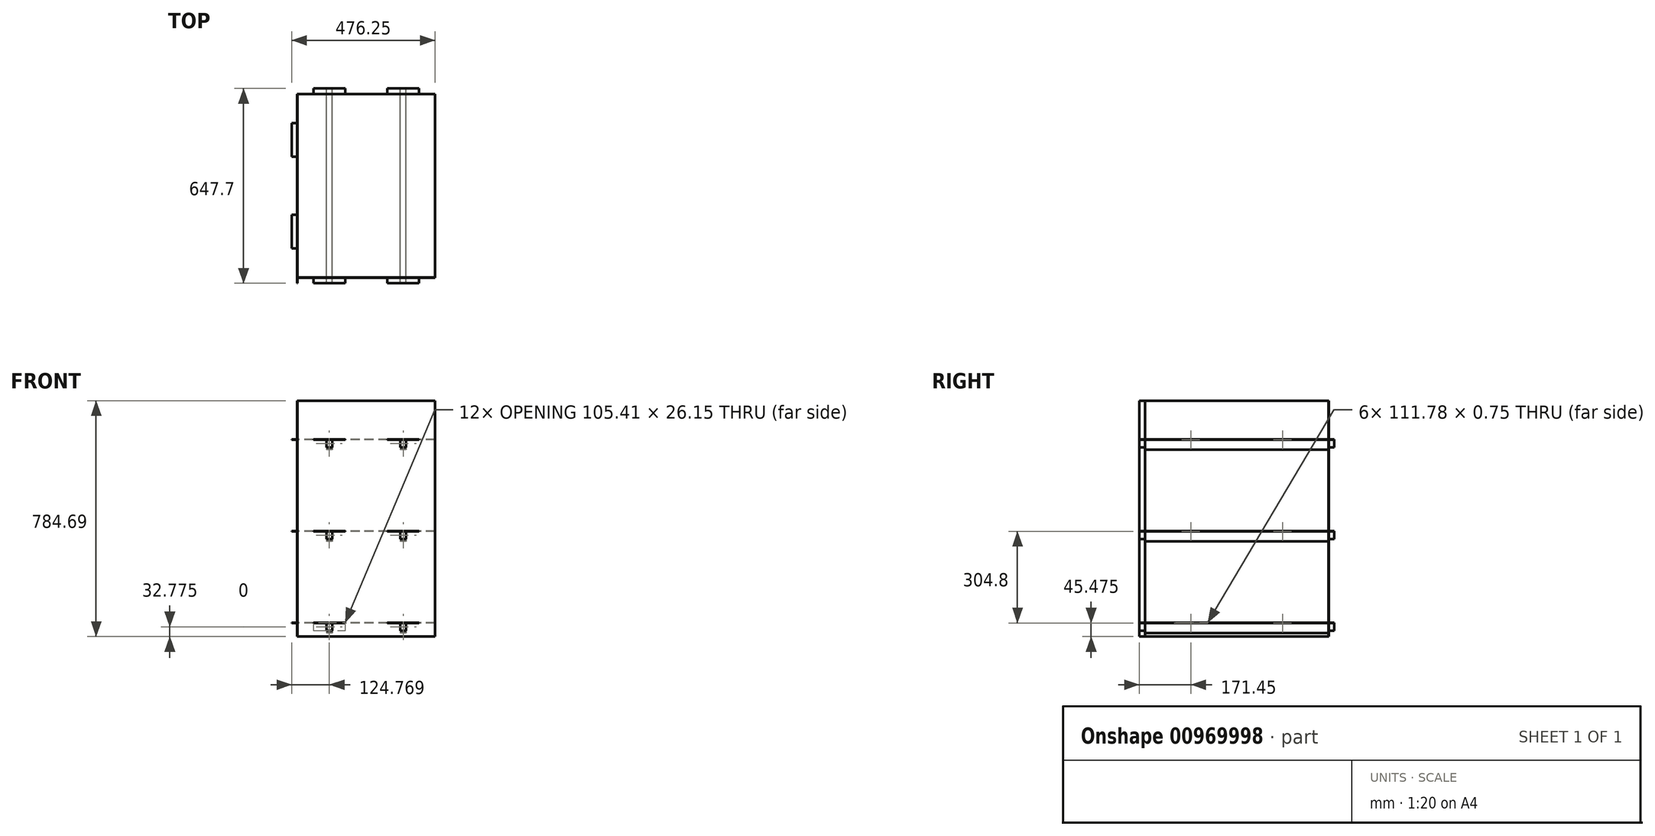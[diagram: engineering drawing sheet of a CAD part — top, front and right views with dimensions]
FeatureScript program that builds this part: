
annotation { "Feature Type Name" : "Feature", "Feature Type Description" : "" }
export const myFeature = defineFeature(function(context is Context, id is Id, definition is map)
    precondition{}
    {
        {
            assignVariable(context, id + "F0", {"name" : "plyT", "anyValue" : 0.75});
        }
        {
            var Q0;
            Q0=qCreatedBy(makeId("Top.planeOp"),FACE);
            var sketch = newSketch(context, id + "F1", { "sketchPlane" : qUnion([Q0])});
            skLineSegment(sketch, "E0", {"start": v(356.12, 0) * mm, "end": v(356.12, 304.8) * mm});
            skLineSegment(sketch, "E1", {"start": v(356.12, 304.8) * mm, "end": v(303.11, 304.8) * mm});
            skLineSegment(sketch, "E2", {"start": v(303.11, 304.8) * mm, "end": v(303.11, 323.85) * mm});
            skLineSegment(sketch, "E3", {"start": v(303.11, 323.85) * mm, "end": v(197.7, 323.85) * mm});
            skLineSegment(sketch, "E4", {"start": v(197.7, 323.85) * mm, "end": v(197.7, 304.8) * mm});
            skLineSegment(sketch, "E5", {"start": v(197.7, 304.8) * mm, "end": v(57.34, 304.8) * mm});
            skLineSegment(sketch, "E6", {"start": v(57.34, 304.8) * mm, "end": v(57.34, 323.85) * mm});
            skLineSegment(sketch, "E7", {"start": v(57.34, 323.85) * mm, "end": v(-48.07, 323.85) * mm});
            skLineSegment(sketch, "E8", {"start": v(-48.07, 323.85) * mm, "end": v(-48.07, 304.8) * mm});
            skLineSegment(sketch, "E9", {"start": v(-48.07, 304.8) * mm, "end": v(-101.08, 304.8) * mm});
            skLineSegment(sketch, "E10", {"start": v(-101.08, 304.8) * mm, "end": v(-101.08, 208.3) * mm});
            skLineSegment(sketch, "E11", {"start": v(-101.08, 208.3) * mm, "end": v(-120.13, 208.3) * mm});
            skLineSegment(sketch, "E12", {"start": v(-120.13, 208.3) * mm, "end": v(-120.13, 96.5) * mm});
            skLineSegment(sketch, "E13", {"start": v(-120.13, 96.5) * mm, "end": v(-101.08, 96.5) * mm});
            skLineSegment(sketch, "E14", {"start": v(-101.08, 96.5) * mm, "end": v(-101.08, 0) * mm});
            skLineSegment(sketch, "E15.MirrorCS", {"start": v(-101.08, -208.3) * mm, "end": v(-120.13, -208.3) * mm});
            skLineSegment(sketch, "E16.MirrorCS", {"start": v(197.7, -323.85) * mm, "end": v(197.7, -304.8) * mm});
            skLineSegment(sketch, "E17.MirrorCS", {"start": v(-120.13, -96.5) * mm, "end": v(-101.08, -96.5) * mm});
            skLineSegment(sketch, "E18.MirrorCS", {"start": v(-101.08, -304.8) * mm, "end": v(-101.08, -208.3) * mm});
            skLineSegment(sketch, "E19.MirrorCS", {"start": v(303.11, -304.8) * mm, "end": v(303.11, -323.85) * mm});
            skLineSegment(sketch, "E20.MirrorCS", {"start": v(-48.07, -323.85) * mm, "end": v(-48.07, -304.8) * mm});
            skLineSegment(sketch, "E21.MirrorCS", {"start": v(356.12, 0) * mm, "end": v(356.12, -304.8) * mm});
            skLineSegment(sketch, "E22.MirrorCS", {"start": v(356.12, -304.8) * mm, "end": v(303.11, -304.8) * mm});
            skLineSegment(sketch, "E23.MirrorCS", {"start": v(57.34, -323.85) * mm, "end": v(-48.07, -323.85) * mm});
            skLineSegment(sketch, "E24.MirrorCS", {"start": v(57.34, -304.8) * mm, "end": v(57.34, -323.85) * mm});
            skLineSegment(sketch, "E25.MirrorCS", {"start": v(-120.13, -208.3) * mm, "end": v(-120.13, -96.5) * mm});
            skLineSegment(sketch, "E26.MirrorCS", {"start": v(197.7, -304.8) * mm, "end": v(57.34, -304.8) * mm});
            skLineSegment(sketch, "E27.MirrorCS", {"start": v(-48.07, -304.8) * mm, "end": v(-101.08, -304.8) * mm});
            skLineSegment(sketch, "E28.MirrorCS", {"start": v(303.11, -323.85) * mm, "end": v(197.7, -323.85) * mm});
            skLineSegment(sketch, "E29.MirrorCS", {"start": v(-101.08, -96.5) * mm, "end": v(-101.08, 0) * mm});
            skSolve(sketch);
        }
        {
            var Q0;
            Q0=makeQuery(id+"F1.imprint","IMPRINT",FACE,{"disambiguationData":[TD([[makeQuery(id+"F1.imprint","IMPRINT",EDGE,{"derivedFrom":sQuery(id+"F1.wireOp",EDGE,"E0")}),1.0]])]});
            extrude(context, id + "F2", {"entities" : qUnion([Q0]), "depth" : (getVariable(context, 'plyT')) * mm, "offsetDistance" : 25.4 * mm});
        }
        {
            var Q0;
            Q0=makeQuery(id+"F2.opExtrude","SWEPT_FACE",FACE,{"disambiguationData":[OSD([sQuery(id+"F1.wireOp",EDGE,"E3")])]});
            var sketch = newSketch(context, id + "F3", { "sketchPlane" : qUnion([Q0])});
            skLineSegment(sketch, "E30.bottom", {"start": v(-259.93, 0) * mm, "end": v(-240.88, 0) * mm});
            skLineSegment(sketch, "E30.top", {"start": v(-259.93, -25.4) * mm, "end": v(-240.88, -25.4) * mm});
            skLineSegment(sketch, "E30.left", {"start": v(-259.93, 0) * mm, "end": v(-259.93, -25.4) * mm});
            skLineSegment(sketch, "E30.right", {"start": v(-240.88, 0) * mm, "end": v(-240.88, -25.4) * mm});
            skLineSegment(sketch, "E31.bottom", {"start": v(-14.16, 0) * mm, "end": v(4.89, 0) * mm});
            skLineSegment(sketch, "E31.top", {"start": v(-14.16, -25.4) * mm, "end": v(4.89, -25.4) * mm});
            skLineSegment(sketch, "E31.left", {"start": v(-14.16, 0) * mm, "end": v(-14.16, -25.4) * mm});
            skLineSegment(sketch, "E31.right", {"start": v(4.89, 0) * mm, "end": v(4.89, -25.4) * mm});
            skLineSegment(sketch, "E32", {"start": v(-303.11, 0) * mm, "end": v(-259.93, 0) * mm, "construction": true});
            skLineSegment(sketch, "E33", {"start": v(-240.88, 0) * mm, "end": v(-197.7, 0) * mm, "construction": true});
            skPoint(sketch, "E34.0", {"position": v(-57.34, 0) * mm});
            skPoint(sketch, "E35.0", {"position": v(48.07, 0) * mm});
            skLineSegment(sketch, "E36", {"start": v(-57.34, 0) * mm, "end": v(-14.16, 0) * mm, "construction": true});
            skLineSegment(sketch, "E37", {"start": v(4.89, 0) * mm, "end": v(48.07, 0) * mm, "construction": true});
            skSolve(sketch);
        }
        {
            var Q0;
            Q0=makeQuery(id+"F3.imprint","IMPRINT",FACE,{"disambiguationData":[TD([[makeQuery(id+"F3.imprint","IMPRINT",EDGE,{"derivedFrom":sQuery(id+"F3.wireOp",EDGE,"E30.bottom")}),-1.0]])]});
            var Q1;
            Q1=makeQuery(id+"F3.imprint","IMPRINT",FACE,{"disambiguationData":[TD([[makeQuery(id+"F3.imprint","IMPRINT",EDGE,{"derivedFrom":sQuery(id+"F3.wireOp",EDGE,"E31.bottom")}),-1.0]])]});
            var Q2;
            Q2=makeQuery(id+"F2.opExtrude","SWEPT_FACE",FACE,{"disambiguationData":[OSD([sQuery(id+"F1.wireOp",EDGE,"E28.MirrorCS")])]});
            extrude(context, id + "F4", {"entities" : qUnion([Q0, Q1]), "endBound" : BoundingType.UP_TO_SURFACE, "oppositeDirection" : true, "depth" : 25.4 * mm, "endBoundEntityFace" : qUnion([Q2]), "offsetDistance" : 25.4 * mm});
        }
        {
            var Q0;
            Q0=makeQuery(id+"F2.opExtrude","SWEPT_FACE",FACE,{"disambiguationData":[OSD([sQuery(id+"F1.wireOp",EDGE,"E5")])]});
            var sketch = newSketch(context, id + "F5", { "sketchPlane" : qUnion([Q0])});
            skLineSegment(sketch, "E38.0", {"start": v(-259.93, -25.4) * mm, "end": v(-240.88, -25.4) * mm});
            skLineSegment(sketch, "E39.0", {"start": v(-14.16, -25.4) * mm, "end": v(4.89, -25.4) * mm});
            skLineSegment(sketch, "E40.top", {"start": v(-259.93, -33.02) * mm, "end": v(-240.88, -33.02) * mm});
            skLineSegment(sketch, "E40.left", {"start": v(-259.93, -25.4) * mm, "end": v(-259.93, -33.02) * mm});
            skLineSegment(sketch, "E40.right", {"start": v(-240.88, -25.4) * mm, "end": v(-240.88, -33.02) * mm});
            skLineSegment(sketch, "E41.top", {"start": v(-14.16, -33.02) * mm, "end": v(4.89, -33.02) * mm});
            skLineSegment(sketch, "E41.left", {"start": v(-14.16, -25.4) * mm, "end": v(-14.16, -33.02) * mm});
            skLineSegment(sketch, "E41.right", {"start": v(4.89, -25.4) * mm, "end": v(4.89, -33.02) * mm});
            skSolve(sketch);
        }
        {
            var Q0;
            Q0=makeQuery(id+"F5.imprint","IMPRINT",FACE,{"disambiguationData":[TD([[makeQuery(id+"F5.imprint","IMPRINT",EDGE,{"derivedFrom":sQuery(id+"F5.wireOp",EDGE,"E38.0")}),-1.0]])]});
            var Q1;
            Q1=makeQuery(id+"F5.imprint","IMPRINT",FACE,{"disambiguationData":[TD([[makeQuery(id+"F5.imprint","IMPRINT",EDGE,{"derivedFrom":sQuery(id+"F5.wireOp",EDGE,"E39.0")}),-1.0]])]});
            var Q2;
            Q2=makeQuery(id+"F2.opExtrude","SWEPT_FACE",FACE,{"disambiguationData":[OSD([sQuery(id+"F1.wireOp",EDGE,"E22.MirrorCS")])]});
            extrude(context, id + "F6", {"entities" : qUnion([Q0, Q1]), "operationType" : NewBodyOperationType.ADD, "endBound" : BoundingType.UP_TO_SURFACE, "oppositeDirection" : true, "depth" : 25.4 * mm, "endBoundEntityFace" : qUnion([Q2]), "offsetDistance" : 25.4 * mm});
        }
        {
            var Q0;
            Q0=makeQuery(id+"F2.opExtrude","SWEPT_BODY",BODY,{"disambiguationData":[OSD([sQuery(id+"F1.wireOp",EDGE,"E0"),sQuery(id+"F1.wireOp",EDGE,"E1"),sQuery(id+"F1.wireOp",EDGE,"E2"),sQuery(id+"F1.wireOp",EDGE,"E3"),sQuery(id+"F1.wireOp",EDGE,"E4"),sQuery(id+"F1.wireOp",EDGE,"E5"),sQuery(id+"F1.wireOp",EDGE,"E6"),sQuery(id+"F1.wireOp",EDGE,"E7"),sQuery(id+"F1.wireOp",EDGE,"E8"),sQuery(id+"F1.wireOp",EDGE,"E9"),sQuery(id+"F1.wireOp",EDGE,"E10"),sQuery(id+"F1.wireOp",EDGE,"E11"),sQuery(id+"F1.wireOp",EDGE,"E12"),sQuery(id+"F1.wireOp",EDGE,"E13"),sQuery(id+"F1.wireOp",EDGE,"E14"),sQuery(id+"F1.wireOp",EDGE,"E15.MirrorCS"),sQuery(id+"F1.wireOp",EDGE,"E16.MirrorCS"),sQuery(id+"F1.wireOp",EDGE,"E17.MirrorCS"),sQuery(id+"F1.wireOp",EDGE,"E18.MirrorCS"),sQuery(id+"F1.wireOp",EDGE,"E19.MirrorCS"),sQuery(id+"F1.wireOp",EDGE,"E20.MirrorCS"),sQuery(id+"F1.wireOp",EDGE,"E21.MirrorCS"),sQuery(id+"F1.wireOp",EDGE,"E22.MirrorCS"),sQuery(id+"F1.wireOp",EDGE,"E23.MirrorCS"),sQuery(id+"F1.wireOp",EDGE,"E24.MirrorCS"),sQuery(id+"F1.wireOp",EDGE,"E25.MirrorCS"),sQuery(id+"F1.wireOp",EDGE,"E26.MirrorCS"),sQuery(id+"F1.wireOp",EDGE,"E27.MirrorCS"),sQuery(id+"F1.wireOp",EDGE,"E28.MirrorCS"),sQuery(id+"F1.wireOp",EDGE,"E29.MirrorCS")])]});
            var Q1;
            Q1=makeQuery(id+"F4.opExtrude","SWEPT_BODY",BODY,{"disambiguationData":[OSD([sQuery(id+"F3.wireOp",EDGE,"E30.bottom"),sQuery(id+"F3.wireOp",EDGE,"E30.top"),sQuery(id+"F3.wireOp",EDGE,"E30.left"),sQuery(id+"F3.wireOp",EDGE,"E30.right")])]});
            var Q2;
            Q2=makeQuery(id+"F4.opExtrude","SWEPT_BODY",BODY,{"disambiguationData":[OSD([sQuery(id+"F3.wireOp",EDGE,"E31.bottom"),sQuery(id+"F3.wireOp",EDGE,"E31.top"),sQuery(id+"F3.wireOp",EDGE,"E31.left"),sQuery(id+"F3.wireOp",EDGE,"E31.right")])]});
            transform(context, id + "F7", {"entities" : qUnion([Q0, Q1, Q2]), "transformType" : TransformType.TRANSLATION_3D, "dx" : 0 * mm, "dy" : 0 * mm, "dz" : -304.8 * mm, "makeCopy" : true});
        }
        {
            var Q0;
            Q0=makeQuery(id+"F7.opPattern","COPY",BODY,{"derivedFrom":makeQuery(id+"F2.opExtrude","SWEPT_BODY",BODY,{"disambiguationData":[OSD([sQuery(id+"F1.wireOp",EDGE,"E0"),sQuery(id+"F1.wireOp",EDGE,"E1"),sQuery(id+"F1.wireOp",EDGE,"E2"),sQuery(id+"F1.wireOp",EDGE,"E3"),sQuery(id+"F1.wireOp",EDGE,"E4"),sQuery(id+"F1.wireOp",EDGE,"E5"),sQuery(id+"F1.wireOp",EDGE,"E6"),sQuery(id+"F1.wireOp",EDGE,"E7"),sQuery(id+"F1.wireOp",EDGE,"E8"),sQuery(id+"F1.wireOp",EDGE,"E9"),sQuery(id+"F1.wireOp",EDGE,"E10"),sQuery(id+"F1.wireOp",EDGE,"E11"),sQuery(id+"F1.wireOp",EDGE,"E12"),sQuery(id+"F1.wireOp",EDGE,"E13"),sQuery(id+"F1.wireOp",EDGE,"E14"),sQuery(id+"F1.wireOp",EDGE,"E15.MirrorCS"),sQuery(id+"F1.wireOp",EDGE,"E16.MirrorCS"),sQuery(id+"F1.wireOp",EDGE,"E17.MirrorCS"),sQuery(id+"F1.wireOp",EDGE,"E18.MirrorCS"),sQuery(id+"F1.wireOp",EDGE,"E19.MirrorCS"),sQuery(id+"F1.wireOp",EDGE,"E20.MirrorCS"),sQuery(id+"F1.wireOp",EDGE,"E21.MirrorCS"),sQuery(id+"F1.wireOp",EDGE,"E22.MirrorCS"),sQuery(id+"F1.wireOp",EDGE,"E23.MirrorCS"),sQuery(id+"F1.wireOp",EDGE,"E24.MirrorCS"),sQuery(id+"F1.wireOp",EDGE,"E25.MirrorCS"),sQuery(id+"F1.wireOp",EDGE,"E26.MirrorCS"),sQuery(id+"F1.wireOp",EDGE,"E27.MirrorCS"),sQuery(id+"F1.wireOp",EDGE,"E28.MirrorCS"),sQuery(id+"F1.wireOp",EDGE,"E29.MirrorCS")])]}),"instanceName":"1"});
            var Q1;
            Q1=makeQuery(id+"F7.opPattern","COPY",BODY,{"derivedFrom":makeQuery(id+"F4.opExtrude","SWEPT_BODY",BODY,{"disambiguationData":[OSD([sQuery(id+"F3.wireOp",EDGE,"E30.bottom"),sQuery(id+"F3.wireOp",EDGE,"E30.top"),sQuery(id+"F3.wireOp",EDGE,"E30.left"),sQuery(id+"F3.wireOp",EDGE,"E30.right")])]}),"instanceName":"1"});
            var Q2;
            Q2=makeQuery(id+"F7.opPattern","COPY",BODY,{"derivedFrom":makeQuery(id+"F4.opExtrude","SWEPT_BODY",BODY,{"disambiguationData":[OSD([sQuery(id+"F3.wireOp",EDGE,"E31.bottom"),sQuery(id+"F3.wireOp",EDGE,"E31.top"),sQuery(id+"F3.wireOp",EDGE,"E31.left"),sQuery(id+"F3.wireOp",EDGE,"E31.right")])]}),"instanceName":"1"});
            transform(context, id + "F8", {"entities" : qUnion([Q0, Q1, Q2]), "transformType" : TransformType.TRANSLATION_3D, "dx" : 0 * mm, "dy" : 0 * mm, "dz" : -304.8 * mm, "makeCopy" : true});
        }
        {
            var Q0;
            Q0=makeQuery(id+"F2.opExtrude","SWEPT_FACE",FACE,{"disambiguationData":[OSD([sQuery(id+"F1.wireOp",EDGE,"E26.MirrorCS")])]});
            var sketch = newSketch(context, id + "F9", { "sketchPlane" : qUnion([Q0])});
            skLineSegment(sketch, "E42.bottom", {"start": v(-101.08, 130) * mm, "end": v(356.12, 130) * mm});
            skLineSegment(sketch, "E42.top", {"start": v(-101.08, -654.7) * mm, "end": v(356.12, -654.7) * mm});
            skLineSegment(sketch, "E42.left", {"start": v(-101.08, 130) * mm, "end": v(-101.08, -654.7) * mm});
            skLineSegment(sketch, "E42.right", {"start": v(356.12, 130) * mm, "end": v(356.12, -654.7) * mm});
            skPoint(sketch, "E43.0", {"position": v(-101.08, 19.05) * mm});
            skSolve(sketch);
        }
        {
            var Q0;
            Q0=makeQuery(id+"F9.imprint","IMPRINT",FACE,{"disambiguationData":[TD([[makeQuery(id+"F9.imprint","IMPRINT",EDGE,{"derivedFrom":sQuery(id+"F9.wireOp",EDGE,"E42.bottom")}),-1.0]])]});
            var Q1;
            {var subQ0=sQuery(id+"F1.wireOp",EDGE,"E26.MirrorCS");Q1=makeQuery(id+"F9.imprint","IMPRINT",FACE,{"disambiguationData":[TD([[makeQuery(id+"F9.imprint","IMPRINT",EDGE,{"derivedFrom":makeQuery(id+"F2.opExtrude","CAP_EDGE",EDGE,{"disambiguationData":[OSD([subQ0])],"isStart":true})}),-1.0]])]});}
            extrude(context, id + "F10", {"entities" : qUnion([Q0, Q1]), "depth" : (getVariable(context, 'plyT')) * mm, "offsetDistance" : 25.4 * mm});
        }
        {
            var Q0;
            Q0=makeQuery(id+"F2.opExtrude","SWEPT_BODY",BODY,{"disambiguationData":[OSD([sQuery(id+"F1.wireOp",EDGE,"E0"),sQuery(id+"F1.wireOp",EDGE,"E1"),sQuery(id+"F1.wireOp",EDGE,"E2"),sQuery(id+"F1.wireOp",EDGE,"E3"),sQuery(id+"F1.wireOp",EDGE,"E4"),sQuery(id+"F1.wireOp",EDGE,"E5"),sQuery(id+"F1.wireOp",EDGE,"E6"),sQuery(id+"F1.wireOp",EDGE,"E7"),sQuery(id+"F1.wireOp",EDGE,"E8"),sQuery(id+"F1.wireOp",EDGE,"E9"),sQuery(id+"F1.wireOp",EDGE,"E10"),sQuery(id+"F1.wireOp",EDGE,"E11"),sQuery(id+"F1.wireOp",EDGE,"E12"),sQuery(id+"F1.wireOp",EDGE,"E13"),sQuery(id+"F1.wireOp",EDGE,"E14"),sQuery(id+"F1.wireOp",EDGE,"E15.MirrorCS"),sQuery(id+"F1.wireOp",EDGE,"E16.MirrorCS"),sQuery(id+"F1.wireOp",EDGE,"E17.MirrorCS"),sQuery(id+"F1.wireOp",EDGE,"E18.MirrorCS"),sQuery(id+"F1.wireOp",EDGE,"E19.MirrorCS"),sQuery(id+"F1.wireOp",EDGE,"E20.MirrorCS"),sQuery(id+"F1.wireOp",EDGE,"E21.MirrorCS"),sQuery(id+"F1.wireOp",EDGE,"E22.MirrorCS"),sQuery(id+"F1.wireOp",EDGE,"E23.MirrorCS"),sQuery(id+"F1.wireOp",EDGE,"E24.MirrorCS"),sQuery(id+"F1.wireOp",EDGE,"E25.MirrorCS"),sQuery(id+"F1.wireOp",EDGE,"E26.MirrorCS"),sQuery(id+"F1.wireOp",EDGE,"E27.MirrorCS"),sQuery(id+"F1.wireOp",EDGE,"E28.MirrorCS"),sQuery(id+"F1.wireOp",EDGE,"E29.MirrorCS")])]});
            var Q1;
            Q1=makeQuery(id+"F7.opPattern","COPY",BODY,{"derivedFrom":makeQuery(id+"F2.opExtrude","SWEPT_BODY",BODY,{"disambiguationData":[OSD([sQuery(id+"F1.wireOp",EDGE,"E0"),sQuery(id+"F1.wireOp",EDGE,"E1"),sQuery(id+"F1.wireOp",EDGE,"E2"),sQuery(id+"F1.wireOp",EDGE,"E3"),sQuery(id+"F1.wireOp",EDGE,"E4"),sQuery(id+"F1.wireOp",EDGE,"E5"),sQuery(id+"F1.wireOp",EDGE,"E6"),sQuery(id+"F1.wireOp",EDGE,"E7"),sQuery(id+"F1.wireOp",EDGE,"E8"),sQuery(id+"F1.wireOp",EDGE,"E9"),sQuery(id+"F1.wireOp",EDGE,"E10"),sQuery(id+"F1.wireOp",EDGE,"E11"),sQuery(id+"F1.wireOp",EDGE,"E12"),sQuery(id+"F1.wireOp",EDGE,"E13"),sQuery(id+"F1.wireOp",EDGE,"E14"),sQuery(id+"F1.wireOp",EDGE,"E15.MirrorCS"),sQuery(id+"F1.wireOp",EDGE,"E16.MirrorCS"),sQuery(id+"F1.wireOp",EDGE,"E17.MirrorCS"),sQuery(id+"F1.wireOp",EDGE,"E18.MirrorCS"),sQuery(id+"F1.wireOp",EDGE,"E19.MirrorCS"),sQuery(id+"F1.wireOp",EDGE,"E20.MirrorCS"),sQuery(id+"F1.wireOp",EDGE,"E21.MirrorCS"),sQuery(id+"F1.wireOp",EDGE,"E22.MirrorCS"),sQuery(id+"F1.wireOp",EDGE,"E23.MirrorCS"),sQuery(id+"F1.wireOp",EDGE,"E24.MirrorCS"),sQuery(id+"F1.wireOp",EDGE,"E25.MirrorCS"),sQuery(id+"F1.wireOp",EDGE,"E26.MirrorCS"),sQuery(id+"F1.wireOp",EDGE,"E27.MirrorCS"),sQuery(id+"F1.wireOp",EDGE,"E28.MirrorCS"),sQuery(id+"F1.wireOp",EDGE,"E29.MirrorCS")])]}),"instanceName":"1"});
            var Q2;
            Q2=makeQuery(id+"F8.opPattern","COPY",BODY,{"derivedFrom":makeQuery(id+"F7.opPattern","COPY",BODY,{"derivedFrom":makeQuery(id+"F2.opExtrude","SWEPT_BODY",BODY,{"disambiguationData":[OSD([sQuery(id+"F1.wireOp",EDGE,"E0"),sQuery(id+"F1.wireOp",EDGE,"E1"),sQuery(id+"F1.wireOp",EDGE,"E2"),sQuery(id+"F1.wireOp",EDGE,"E3"),sQuery(id+"F1.wireOp",EDGE,"E4"),sQuery(id+"F1.wireOp",EDGE,"E5"),sQuery(id+"F1.wireOp",EDGE,"E6"),sQuery(id+"F1.wireOp",EDGE,"E7"),sQuery(id+"F1.wireOp",EDGE,"E8"),sQuery(id+"F1.wireOp",EDGE,"E9"),sQuery(id+"F1.wireOp",EDGE,"E10"),sQuery(id+"F1.wireOp",EDGE,"E11"),sQuery(id+"F1.wireOp",EDGE,"E12"),sQuery(id+"F1.wireOp",EDGE,"E13"),sQuery(id+"F1.wireOp",EDGE,"E14"),sQuery(id+"F1.wireOp",EDGE,"E15.MirrorCS"),sQuery(id+"F1.wireOp",EDGE,"E16.MirrorCS"),sQuery(id+"F1.wireOp",EDGE,"E17.MirrorCS"),sQuery(id+"F1.wireOp",EDGE,"E18.MirrorCS"),sQuery(id+"F1.wireOp",EDGE,"E19.MirrorCS"),sQuery(id+"F1.wireOp",EDGE,"E20.MirrorCS"),sQuery(id+"F1.wireOp",EDGE,"E21.MirrorCS"),sQuery(id+"F1.wireOp",EDGE,"E22.MirrorCS"),sQuery(id+"F1.wireOp",EDGE,"E23.MirrorCS"),sQuery(id+"F1.wireOp",EDGE,"E24.MirrorCS"),sQuery(id+"F1.wireOp",EDGE,"E25.MirrorCS"),sQuery(id+"F1.wireOp",EDGE,"E26.MirrorCS"),sQuery(id+"F1.wireOp",EDGE,"E27.MirrorCS"),sQuery(id+"F1.wireOp",EDGE,"E28.MirrorCS"),sQuery(id+"F1.wireOp",EDGE,"E29.MirrorCS")])]}),"instanceName":"1"}),"instanceName":"1"});
            var Q3;
            Q3=makeQuery(id+"F4.opExtrude","SWEPT_BODY",BODY,{"disambiguationData":[OSD([sQuery(id+"F3.wireOp",EDGE,"E31.bottom"),sQuery(id+"F3.wireOp",EDGE,"E31.top"),sQuery(id+"F3.wireOp",EDGE,"E31.left"),sQuery(id+"F3.wireOp",EDGE,"E31.right")])]});
            var Q4;
            Q4=makeQuery(id+"F4.opExtrude","SWEPT_BODY",BODY,{"disambiguationData":[OSD([sQuery(id+"F3.wireOp",EDGE,"E30.bottom"),sQuery(id+"F3.wireOp",EDGE,"E30.top"),sQuery(id+"F3.wireOp",EDGE,"E30.left"),sQuery(id+"F3.wireOp",EDGE,"E30.right")])]});
            var Q5;
            Q5=makeQuery(id+"F7.opPattern","COPY",BODY,{"derivedFrom":makeQuery(id+"F4.opExtrude","SWEPT_BODY",BODY,{"disambiguationData":[OSD([sQuery(id+"F3.wireOp",EDGE,"E31.bottom"),sQuery(id+"F3.wireOp",EDGE,"E31.top"),sQuery(id+"F3.wireOp",EDGE,"E31.left"),sQuery(id+"F3.wireOp",EDGE,"E31.right")])]}),"instanceName":"1"});
            var Q6;
            Q6=makeQuery(id+"F7.opPattern","COPY",BODY,{"derivedFrom":makeQuery(id+"F4.opExtrude","SWEPT_BODY",BODY,{"disambiguationData":[OSD([sQuery(id+"F3.wireOp",EDGE,"E30.bottom"),sQuery(id+"F3.wireOp",EDGE,"E30.top"),sQuery(id+"F3.wireOp",EDGE,"E30.left"),sQuery(id+"F3.wireOp",EDGE,"E30.right")])]}),"instanceName":"1"});
            var Q7;
            Q7=makeQuery(id+"F8.opPattern","COPY",BODY,{"derivedFrom":makeQuery(id+"F7.opPattern","COPY",BODY,{"derivedFrom":makeQuery(id+"F4.opExtrude","SWEPT_BODY",BODY,{"disambiguationData":[OSD([sQuery(id+"F3.wireOp",EDGE,"E31.bottom"),sQuery(id+"F3.wireOp",EDGE,"E31.top"),sQuery(id+"F3.wireOp",EDGE,"E31.left"),sQuery(id+"F3.wireOp",EDGE,"E31.right")])]}),"instanceName":"1"}),"instanceName":"1"});
            var Q8;
            Q8=makeQuery(id+"F8.opPattern","COPY",BODY,{"derivedFrom":makeQuery(id+"F7.opPattern","COPY",BODY,{"derivedFrom":makeQuery(id+"F4.opExtrude","SWEPT_BODY",BODY,{"disambiguationData":[OSD([sQuery(id+"F3.wireOp",EDGE,"E30.bottom"),sQuery(id+"F3.wireOp",EDGE,"E30.top"),sQuery(id+"F3.wireOp",EDGE,"E30.left"),sQuery(id+"F3.wireOp",EDGE,"E30.right")])]}),"instanceName":"1"}),"instanceName":"1"});
            var Q9;
            Q9=makeQuery(id+"F10.opExtrude","SWEPT_BODY",BODY,{"disambiguationData":[OSD([sQuery(id+"F9.wireOp",EDGE,"E42.bottom"),sQuery(id+"F9.wireOp",EDGE,"E42.top"),sQuery(id+"F9.wireOp",EDGE,"E42.left"),sQuery(id+"F9.wireOp",EDGE,"E42.right")])]});
            booleanBodies(context, id + "F11", {"operationType" : BooleanOperationType.SUBTRACTION, "tools" : qUnion([Q0, Q1, Q2, Q3, Q4, Q5, Q6, Q7, Q8]), "targets" : qUnion([Q9]), "keepTools" : true});
        }
        {
            var Q0;
            Q0=makeQuery(id+"F10.opExtrude","SWEPT_BODY",BODY,{"disambiguationData":[OSD([sQuery(id+"F9.wireOp",EDGE,"E42.bottom"),sQuery(id+"F9.wireOp",EDGE,"E42.top"),sQuery(id+"F9.wireOp",EDGE,"E42.left"),sQuery(id+"F9.wireOp",EDGE,"E42.right")])]});
            var Q1;
            Q1=qCreatedBy(makeId("Front.planeOp"),FACE);
            mirror(context, id + "F12", {"entities" : qUnion([Q0]), "mirrorPlane" : qUnion([Q1])});
        }
        {
            var Q0;
            Q0=makeQuery(id+"F12.opPattern","COPY",FACE,{"derivedFrom":makeQuery(id+"F10.opExtrude","SWEPT_FACE",FACE,{"disambiguationData":[OSD([sQuery(id+"F9.wireOp",EDGE,"E42.left")])]}),"instanceName":"1"});
            var sketch = newSketch(context, id + "F13", { "sketchPlane" : qUnion([Q0])});
            skPoint(sketch, "E44.0", {"position": v(-323.85, -654.7) * mm});
            skPoint(sketch, "E45.0", {"position": v(323.85, 130) * mm});
            skLineSegment(sketch, "E46.bottom", {"start": v(-323.85, -654.7) * mm, "end": v(323.85, -654.7) * mm});
            skLineSegment(sketch, "E46.top", {"start": v(-323.85, 130) * mm, "end": v(323.85, 130) * mm});
            skLineSegment(sketch, "E46.left", {"start": v(-323.85, -654.7) * mm, "end": v(-323.85, 130) * mm});
            skLineSegment(sketch, "E46.right", {"start": v(323.85, -654.7) * mm, "end": v(323.85, 130) * mm});
            skSolve(sketch);
        }
        {
            var Q0;
            {var subQ2=sQuery(id+"F13.wireOp",EDGE,"E46.right");Q0=makeQuery(id+"F13.imprint","IMPRINT",FACE,{"disambiguationData":[TD([[makeQuery(id+"F13.imprint","IMPRINT",EDGE,{"derivedFrom":subQ2}),1.0]])]});}
            var Q1;
            {var subQ2=sQuery(id+"F13.wireOp",EDGE,"E46.left");Q1=makeQuery(id+"F13.imprint","IMPRINT",FACE,{"disambiguationData":[TD([[makeQuery(id+"F13.imprint","IMPRINT",EDGE,{"derivedFrom":subQ2}),1.0]])]});}
            extrude(context, id + "F14", {"entities" : qUnion([Q0, Q1]), "depth" : (getVariable(context, 'plyT')) * mm, "offsetDistance" : 25.4 * mm});
        }
        {
            var Q0;
            Q0=makeQuery(id+"F2.opExtrude","SWEPT_BODY",BODY,{"disambiguationData":[OSD([sQuery(id+"F1.wireOp",EDGE,"E0"),sQuery(id+"F1.wireOp",EDGE,"E1"),sQuery(id+"F1.wireOp",EDGE,"E2"),sQuery(id+"F1.wireOp",EDGE,"E3"),sQuery(id+"F1.wireOp",EDGE,"E4"),sQuery(id+"F1.wireOp",EDGE,"E5"),sQuery(id+"F1.wireOp",EDGE,"E6"),sQuery(id+"F1.wireOp",EDGE,"E7"),sQuery(id+"F1.wireOp",EDGE,"E8"),sQuery(id+"F1.wireOp",EDGE,"E9"),sQuery(id+"F1.wireOp",EDGE,"E10"),sQuery(id+"F1.wireOp",EDGE,"E11"),sQuery(id+"F1.wireOp",EDGE,"E12"),sQuery(id+"F1.wireOp",EDGE,"E13"),sQuery(id+"F1.wireOp",EDGE,"E14"),sQuery(id+"F1.wireOp",EDGE,"E15.MirrorCS"),sQuery(id+"F1.wireOp",EDGE,"E16.MirrorCS"),sQuery(id+"F1.wireOp",EDGE,"E17.MirrorCS"),sQuery(id+"F1.wireOp",EDGE,"E18.MirrorCS"),sQuery(id+"F1.wireOp",EDGE,"E19.MirrorCS"),sQuery(id+"F1.wireOp",EDGE,"E20.MirrorCS"),sQuery(id+"F1.wireOp",EDGE,"E21.MirrorCS"),sQuery(id+"F1.wireOp",EDGE,"E22.MirrorCS"),sQuery(id+"F1.wireOp",EDGE,"E23.MirrorCS"),sQuery(id+"F1.wireOp",EDGE,"E24.MirrorCS"),sQuery(id+"F1.wireOp",EDGE,"E25.MirrorCS"),sQuery(id+"F1.wireOp",EDGE,"E26.MirrorCS"),sQuery(id+"F1.wireOp",EDGE,"E27.MirrorCS"),sQuery(id+"F1.wireOp",EDGE,"E28.MirrorCS"),sQuery(id+"F1.wireOp",EDGE,"E29.MirrorCS")])]});
            var Q1;
            Q1=makeQuery(id+"F7.opPattern","COPY",BODY,{"derivedFrom":makeQuery(id+"F2.opExtrude","SWEPT_BODY",BODY,{"disambiguationData":[OSD([sQuery(id+"F1.wireOp",EDGE,"E0"),sQuery(id+"F1.wireOp",EDGE,"E1"),sQuery(id+"F1.wireOp",EDGE,"E2"),sQuery(id+"F1.wireOp",EDGE,"E3"),sQuery(id+"F1.wireOp",EDGE,"E4"),sQuery(id+"F1.wireOp",EDGE,"E5"),sQuery(id+"F1.wireOp",EDGE,"E6"),sQuery(id+"F1.wireOp",EDGE,"E7"),sQuery(id+"F1.wireOp",EDGE,"E8"),sQuery(id+"F1.wireOp",EDGE,"E9"),sQuery(id+"F1.wireOp",EDGE,"E10"),sQuery(id+"F1.wireOp",EDGE,"E11"),sQuery(id+"F1.wireOp",EDGE,"E12"),sQuery(id+"F1.wireOp",EDGE,"E13"),sQuery(id+"F1.wireOp",EDGE,"E14"),sQuery(id+"F1.wireOp",EDGE,"E15.MirrorCS"),sQuery(id+"F1.wireOp",EDGE,"E16.MirrorCS"),sQuery(id+"F1.wireOp",EDGE,"E17.MirrorCS"),sQuery(id+"F1.wireOp",EDGE,"E18.MirrorCS"),sQuery(id+"F1.wireOp",EDGE,"E19.MirrorCS"),sQuery(id+"F1.wireOp",EDGE,"E20.MirrorCS"),sQuery(id+"F1.wireOp",EDGE,"E21.MirrorCS"),sQuery(id+"F1.wireOp",EDGE,"E22.MirrorCS"),sQuery(id+"F1.wireOp",EDGE,"E23.MirrorCS"),sQuery(id+"F1.wireOp",EDGE,"E24.MirrorCS"),sQuery(id+"F1.wireOp",EDGE,"E25.MirrorCS"),sQuery(id+"F1.wireOp",EDGE,"E26.MirrorCS"),sQuery(id+"F1.wireOp",EDGE,"E27.MirrorCS"),sQuery(id+"F1.wireOp",EDGE,"E28.MirrorCS"),sQuery(id+"F1.wireOp",EDGE,"E29.MirrorCS")])]}),"instanceName":"1"});
            var Q2;
            Q2=makeQuery(id+"F8.opPattern","COPY",BODY,{"derivedFrom":makeQuery(id+"F7.opPattern","COPY",BODY,{"derivedFrom":makeQuery(id+"F2.opExtrude","SWEPT_BODY",BODY,{"disambiguationData":[OSD([sQuery(id+"F1.wireOp",EDGE,"E0"),sQuery(id+"F1.wireOp",EDGE,"E1"),sQuery(id+"F1.wireOp",EDGE,"E2"),sQuery(id+"F1.wireOp",EDGE,"E3"),sQuery(id+"F1.wireOp",EDGE,"E4"),sQuery(id+"F1.wireOp",EDGE,"E5"),sQuery(id+"F1.wireOp",EDGE,"E6"),sQuery(id+"F1.wireOp",EDGE,"E7"),sQuery(id+"F1.wireOp",EDGE,"E8"),sQuery(id+"F1.wireOp",EDGE,"E9"),sQuery(id+"F1.wireOp",EDGE,"E10"),sQuery(id+"F1.wireOp",EDGE,"E11"),sQuery(id+"F1.wireOp",EDGE,"E12"),sQuery(id+"F1.wireOp",EDGE,"E13"),sQuery(id+"F1.wireOp",EDGE,"E14"),sQuery(id+"F1.wireOp",EDGE,"E15.MirrorCS"),sQuery(id+"F1.wireOp",EDGE,"E16.MirrorCS"),sQuery(id+"F1.wireOp",EDGE,"E17.MirrorCS"),sQuery(id+"F1.wireOp",EDGE,"E18.MirrorCS"),sQuery(id+"F1.wireOp",EDGE,"E19.MirrorCS"),sQuery(id+"F1.wireOp",EDGE,"E20.MirrorCS"),sQuery(id+"F1.wireOp",EDGE,"E21.MirrorCS"),sQuery(id+"F1.wireOp",EDGE,"E22.MirrorCS"),sQuery(id+"F1.wireOp",EDGE,"E23.MirrorCS"),sQuery(id+"F1.wireOp",EDGE,"E24.MirrorCS"),sQuery(id+"F1.wireOp",EDGE,"E25.MirrorCS"),sQuery(id+"F1.wireOp",EDGE,"E26.MirrorCS"),sQuery(id+"F1.wireOp",EDGE,"E27.MirrorCS"),sQuery(id+"F1.wireOp",EDGE,"E28.MirrorCS"),sQuery(id+"F1.wireOp",EDGE,"E29.MirrorCS")])]}),"instanceName":"1"}),"instanceName":"1"});
            var Q3;
            Q3=makeQuery(id+"F14.opExtrude","SWEPT_BODY",BODY,{"disambiguationData":[OSD([sQuery(id+"F9.wireOp",EDGE,"E42.left"),sQuery(id+"F13.wireOp",EDGE,"E46.bottom"),sQuery(id+"F13.wireOp",EDGE,"E46.top"),sQuery(id+"F13.wireOp",EDGE,"E46.right")])]});
            booleanBodies(context, id + "F15", {"operationType" : BooleanOperationType.SUBTRACTION, "tools" : qUnion([Q0, Q1, Q2]), "targets" : qUnion([Q3]), "keepTools" : true});
        }
    });
